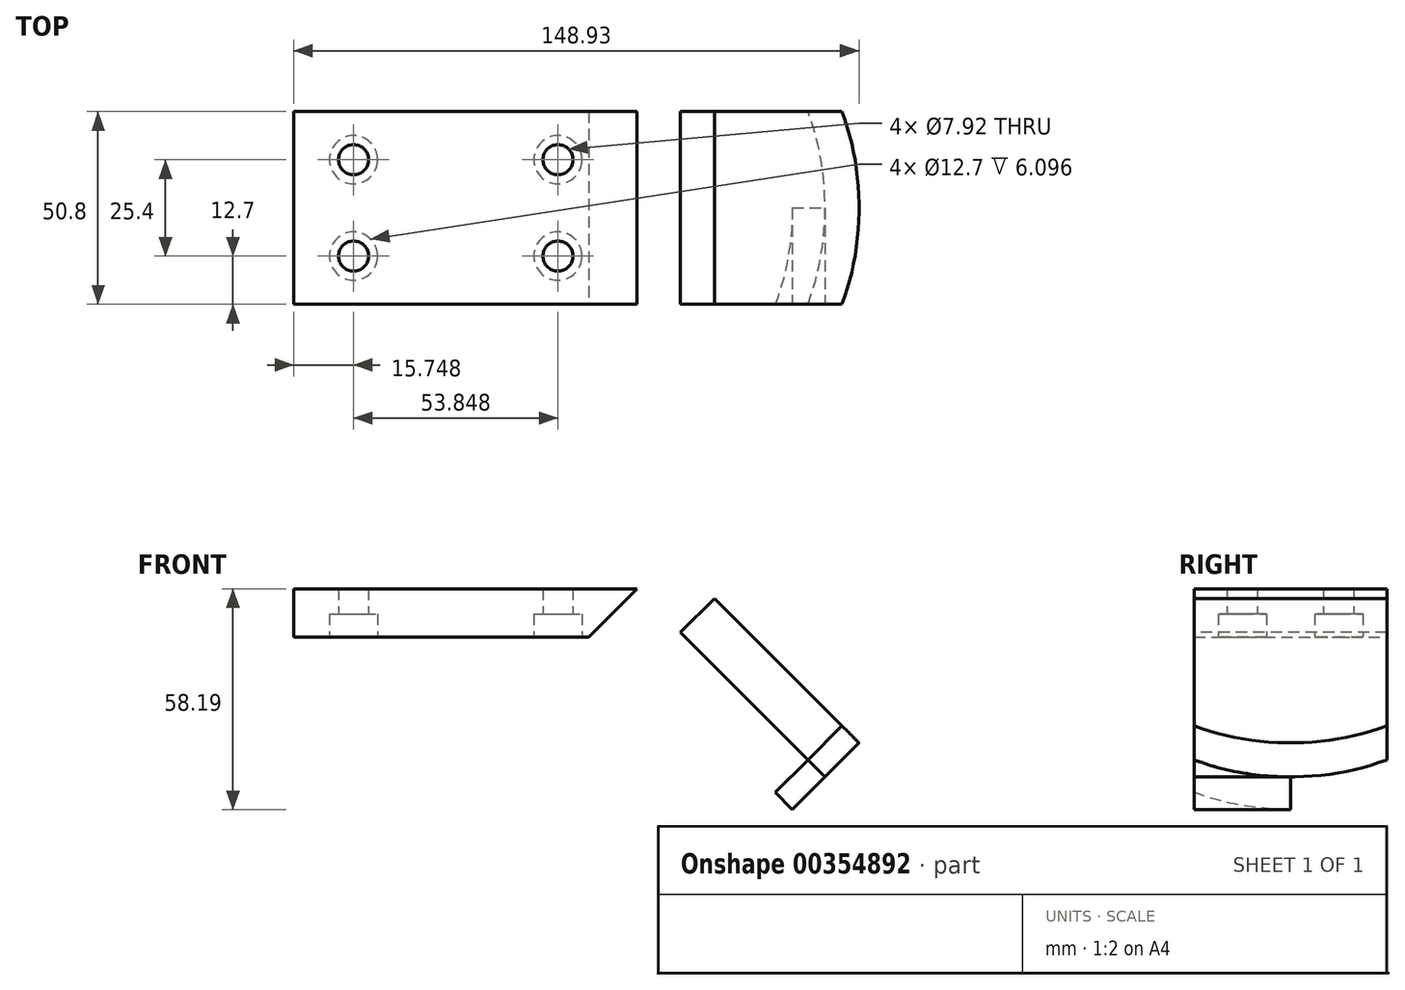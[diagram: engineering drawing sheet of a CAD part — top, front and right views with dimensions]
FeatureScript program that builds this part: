
annotation { "Feature Type Name" : "Feature", "Feature Type Description" : "" }
export const myFeature = defineFeature(function(context is Context, id is Id, definition is map)
    precondition{}
    {
        {
            var Q0;
            Q0=qCreatedBy(makeId("Top.planeOp"),FACE);
            var sketch = newSketch(context, id + "F0", { "sketchPlane" : qUnion([Q0])});
            skLineSegment(sketch, "E0.bottom", {"start": v(0, 0) * mm, "end": v(85.85, 0) * mm});
            skLineSegment(sketch, "E0.top", {"start": v(0, 50.8) * mm, "end": v(85.85, 50.8) * mm});
            skLineSegment(sketch, "E0.left", {"start": v(0, 0) * mm, "end": v(0, 50.8) * mm});
            skLineSegment(sketch, "E0.right", {"start": v(85.85, 0) * mm, "end": v(85.85, 50.8) * mm});
            skLineSegment(sketch, "E1.bottom", {"start": v(15.75, 38.1) * mm, "end": v(69.6, 38.1) * mm, "construction": true});
            skLineSegment(sketch, "E1.top", {"start": v(15.75, 12.7) * mm, "end": v(69.6, 12.7) * mm, "construction": true});
            skLineSegment(sketch, "E1.left", {"start": v(15.75, 38.1) * mm, "end": v(15.75, 12.7) * mm, "construction": true});
            skLineSegment(sketch, "E1.right", {"start": v(69.6, 38.1) * mm, "end": v(69.6, 12.7) * mm, "construction": true});
            skSolve(sketch);
        }
        {
            var Q0;
            Q0=makeQuery(id+"F0.imprint","IMPRINT",FACE,{"disambiguationData":[TD([[makeQuery(id+"F0.imprint","IMPRINT",EDGE,{"derivedFrom":sQuery(id+"F0.wireOp",EDGE,"E0.bottom")}),1.0]])]});
            extrude(context, id + "F1", {"entities" : qUnion([Q0]), "oppositeDirection" : true, "depth" : 12.7 * mm});
        }
        {
            var Q0;
            Q0=makeQuery(id+"F1.opExtrude","CAP_FACE",FACE,{"disambiguationData":[OSD([sQuery(id+"F0.wireOp",EDGE,"E0.bottom"),sQuery(id+"F0.wireOp",EDGE,"E0.top"),sQuery(id+"F0.wireOp",EDGE,"E0.left"),sQuery(id+"F0.wireOp",EDGE,"E0.right")])],"isStart":false});
            var sketch = newSketch(context, id + "F2", { "sketchPlane" : qUnion([Q0])});
            skCircle(sketch, "E2", {"center": v(15.75, -12.7) * mm, "radius": 10.87 * mm});
            skCircle(sketch, "E3", {"center": v(69.6, -12.7) * mm, "radius": 8.9 * mm});
            skCircle(sketch, "E4", {"center": v(15.75, -38.1) * mm, "radius": 10.28 * mm});
            skCircle(sketch, "E5", {"center": v(69.6, -38.1) * mm, "radius": 10.72 * mm});
            skSolve(sketch);
        }
        {
            var Q0;
            Q0=sQuery(id+"F2.wireOp",VERTEX,"E3.center");
            var Q1;
            Q1=sQuery(id+"F2.wireOp",VERTEX,"E2.center");
            var Q2;
            Q2=sQuery(id+"F2.wireOp",VERTEX,"E4.center");
            var Q3;
            Q3=sQuery(id+"F2.wireOp",VERTEX,"E5.center");
            var Q4;
            Q4=makeQuery(id+"F1.opExtrude","SWEPT_BODY",BODY,{"disambiguationData":[OSD([sQuery(id+"F0.wireOp",EDGE,"E0.bottom"),sQuery(id+"F0.wireOp",EDGE,"E0.top"),sQuery(id+"F0.wireOp",EDGE,"E0.left"),sQuery(id+"F0.wireOp",EDGE,"E0.right")])]});
            hole(context, id + "F3", {"style" : HoleStyle.C_BORE, "endStyle" : HoleEndStyle.THROUGH, "holeDiameter" : 7.92 * mm, "cBoreDiameter" : 12.7 * mm, "cBoreDepth" : 6.1 * mm, "isTappedThrough" : true, "tappedDepth" : 12.7 * mm, "tapClearance" : 3, "locations" : qUnion([Q0, Q1, Q2, Q3]), "scope" : qUnion([Q4])});
        }
        {
            var Q0;
            Q0=qCreatedBy(makeId("Front.planeOp"),FACE);
            var sketch = newSketch(context, id + "F4", { "sketchPlane" : qUnion([Q0])});
            skLineSegment(sketch, "E6", {"start": v(85.85, -12.7) * mm, "end": v(131.34, -58.19) * mm});
            skLineSegment(sketch, "E7", {"start": v(90.38, 0) * mm, "end": v(139.95, -49.57) * mm});
            skLineSegment(sketch, "E8", {"start": v(90.38, 0) * mm, "end": v(85.85, 0) * mm});
            skLineSegment(sketch, "E9", {"start": v(139.95, -49.57) * mm, "end": v(131.34, -58.19) * mm});
            skLineSegment(sketch, "E10", {"start": v(85.85, 0) * mm, "end": v(85.85, -12.7) * mm});
            skSolve(sketch);
        }
        {
            var Q0;
            Q0 = qSketchRegion(id + "F4", true);
            extrude(context, id + "F5", {"entities" : qUnion([Q0]), "operationType" : NewBodyOperationType.ADD, "oppositeDirection" : true, "depth" : 50.8 * mm});
        }
        {
            var Q0;
            Q0=makeQuery(id+"F5.opExtrude","SWEPT_FACE",FACE,{"disambiguationData":[OSD([sQuery(id+"F4.wireOp",EDGE,"E7")])]});
            var sketch = newSketch(context, id + "F6", { "sketchPlane" : qUnion([Q0])});
            skLineSegment(sketch, "E11", {"start": v(0, -80.17) * mm, "end": v(50.8, -80.17) * mm, "construction": true});
            skArc(sketch, "E12", {"start": v(25.4, -134.01) * mm, "mid": v(38.5, -132.4) * mm, "end": v(50.8, -127.65) * mm});
            skArc(sketch, "E13", {"start": v(25.4, -134.01) * mm, "mid": v(12.3, -132.4) * mm, "end": v(0, -127.65) * mm});
            skSolve(sketch);
        }
        {
            var Q0;
            {var subQ0=sQuery(id+"F6.wireOp",EDGE,"E12");Q0=makeQuery(id+"F6.imprint","IMPRINT",FACE,{"disambiguationData":[TD([[makeQuery(id+"F6.imprint","IMPRINT",EDGE,{"derivedFrom":subQ0}),-1.0]])]});}
            var Q1;
            {var subQ0=sQuery(id+"F6.wireOp",EDGE,"E13");Q1=makeQuery(id+"F6.imprint","IMPRINT",FACE,{"disambiguationData":[TD([[makeQuery(id+"F6.imprint","IMPRINT",EDGE,{"derivedFrom":subQ0}),1.0]])]});}
            extrude(context, id + "F7", {"entities" : qUnion([Q0, Q1]), "operationType" : NewBodyOperationType.REMOVE, "oppositeDirection" : true, "depth" : 25.4 * mm});
        }
        {
            var Q0;
            {var subQ4=sQuery(id+"F6.wireOp",EDGE,"E12");Q0=makeQuery(id+"F6.imprint","IMPRINT",FACE,{"disambiguationData":[TD([[makeQuery(id+"F6.imprint","IMPRINT",EDGE,{"derivedFrom":subQ4}),1.0]])]});}
            var sketch = newSketch(context, id + "F8", { "sketchPlane" : qUnion([Q0])});
            skLineSegment(sketch, "E14", {"start": v(0, -127.65) * mm, "end": v(50.8, -127.65) * mm});
            skSolve(sketch);
        }
        {
            var Q0;
            Q0=makeQuery(id+"F8.imprint","IMPRINT",FACE,{"disambiguationData":[TD([[makeQuery(id+"F8.imprint","IMPRINT",EDGE,{"derivedFrom":sQuery(id+"F8.wireOp",EDGE,"E14")}),-1.0]])]});
            extrude(context, id + "F9", {"entities" : qUnion([Q0]), "operationType" : NewBodyOperationType.ADD, "depth" : 12.7 * mm});
        }
        {
            var Q0;
            {var subQ4=sQuery(id+"F6.wireOp",EDGE,"E12");Q0=makeQuery(id+"F6.imprint","IMPRINT",FACE,{"disambiguationData":[TD([[makeQuery(id+"F6.imprint","IMPRINT",EDGE,{"derivedFrom":subQ4}),1.0]])]});}
            var sketch = newSketch(context, id + "F10", { "sketchPlane" : qUnion([Q0])});
            skLineSegment(sketch, "E15", {"start": v(0, -80.17) * mm, "end": v(0, -127.65) * mm});
            skLineSegment(sketch, "E16", {"start": v(0, -127.65) * mm, "end": v(50.8, -127.65) * mm});
            skLineSegment(sketch, "E17", {"start": v(50.8, -127.65) * mm, "end": v(50.8, -80.17) * mm});
            skLineSegment(sketch, "E18", {"start": v(50.8, -80.17) * mm, "end": v(0, -80.17) * mm});
            skSolve(sketch);
        }
        {
            var Q0;
            Q0 = qSketchRegion(id + "F10", true);
            extrude(context, id + "F11", {"entities" : qUnion([Q0]), "operationType" : NewBodyOperationType.ADD, "depth" : 12.7 * mm});
        }
        {
            var Q0;
            Q0=makeQuery(id+"F11.opExtrude","SWEPT_FACE",FACE,{"disambiguationData":[OSD([sQuery(id+"F10.wireOp",EDGE,"E18")])]});
            var sketch = newSketch(context, id + "F12", { "sketchPlane" : qUnion([Q0])});
            skLineSegment(sketch, "E19", {"start": v(76.6, 35.05) * mm, "end": v(70.51, 35.05) * mm});
            skLineSegment(sketch, "E20", {"start": v(70.51, 35.05) * mm, "end": v(70.51, 41.15) * mm});
            skLineSegment(sketch, "E21", {"start": v(70.51, 41.15) * mm, "end": v(63.9, 41.15) * mm});
            skLineSegment(sketch, "E22", {"start": v(63.9, 41.15) * mm, "end": v(63.9, 9.65) * mm});
            skLineSegment(sketch, "E23", {"start": v(63.9, 9.65) * mm, "end": v(70.51, 9.65) * mm});
            skLineSegment(sketch, "E24", {"start": v(70.51, 9.65) * mm, "end": v(70.51, 15.75) * mm});
            skLineSegment(sketch, "E25", {"start": v(70.51, 15.75) * mm, "end": v(76.6, 15.75) * mm});
            skLineSegment(sketch, "E26", {"start": v(76.6, 35.05) * mm, "end": v(76.6, 15.75) * mm});
            skSolve(sketch);
        }
        {
            var Q0;
            Q0=makeQuery(id+"F12.imprint","IMPRINT",FACE,{"disambiguationData":[TD([[makeQuery(id+"F12.imprint","IMPRINT",EDGE,{"derivedFrom":sQuery(id+"F12.wireOp",EDGE,"E19")}),1.0]])]});
            extrude(context, id + "F13", {"entities" : qUnion([Q0]), "operationType" : NewBodyOperationType.REMOVE, "endBound" : BoundingType.THROUGH_ALL, "oppositeDirection" : true, "depth" : 25.4 * mm});
        }
    });
